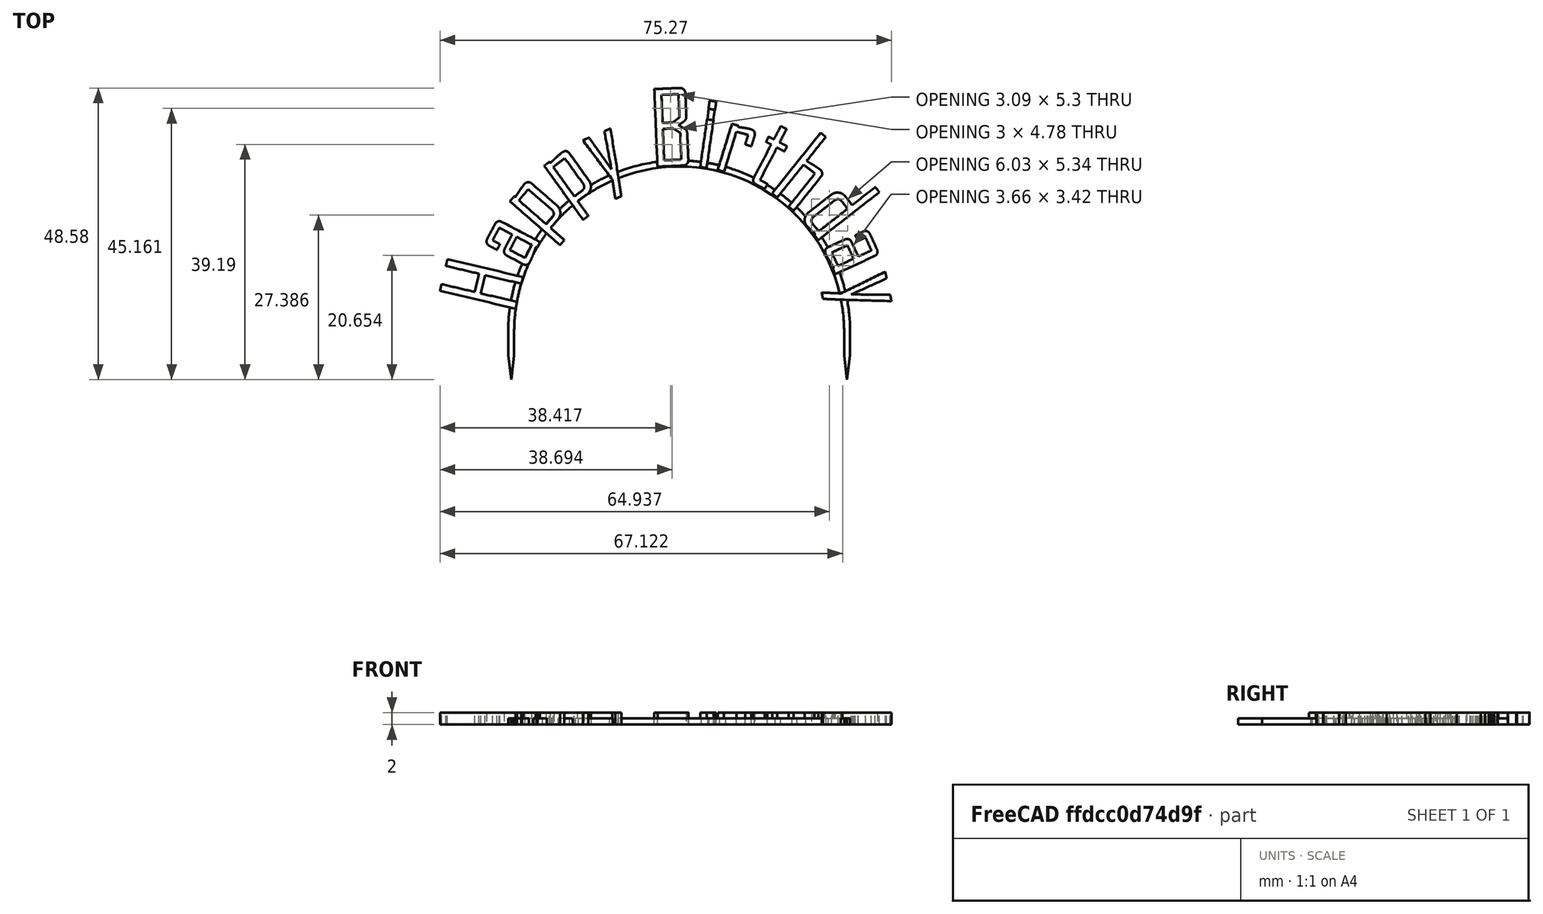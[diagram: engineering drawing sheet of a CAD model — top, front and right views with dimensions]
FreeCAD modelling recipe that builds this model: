
FCSTD DOCUMENT  (FreeCAD 0.20R29177 (Git))
Label: cake-topper-birthday
License: All rights reserved
LicenseURL: http://en.wikipedia.org/wiki/All_rights_reserved
objects: Part::Feature×21, Sketcher::SketchObject×4, PartDesign::Pad×4, App::TextDocument×1, Spreadsheet::Sheet×1, PartDesign::Plane×1, App::Part×1, PartDesign::Body×1, Mesh::Feature×1
note: 35 computed .brp shape members not serialized (recipe doc carries the construction recipe); baked Part::Feature solids carry a one-line shape summary decoded from their .brp

FEATURE [App::TextDocument] Text_document  label="Text document"
FEATURE [Spreadsheet::Sheet] Spreadsheet
  cells = A1=Text height; B1=text_h; C1(dim_text_h)==2mm; A2=Text offset x; B2=text_x; C2(dim_text_x)==-105mm; A3=Text offset y; B3=text_y; C3(dim_text_y)==177.5mm; A4=Scaffold height; B4=scaffold_h; C4(dim_scaffold_h)==1mm; A5=Scaffold width; B5=scaffold_w; C5(dim_scaffold_w)==1mm; A6=Scaffold inner radius; B6=scaffold_ir; C6(dim_scaffold_ir)==27.5mm; A7=Scaffold outer radius; B7=scaffold_or; C7(dim_scaffold_or)==dim_scaffold_ir + dim_scaffold_w; A8=Tines length; B8=tine_l; C8(dim_tine_l)==4mm; A9=Tines shaft length; B9=tine_shaft_l; C9(dim_tine_shaft_l)==4mm
FEATURE [PartDesign::Plane] DatumPlane  label="BaseXYDatumPlane"
  Length = 89.3224
  MapMode = 5
  ResizeMode = 0
  Support = -> [XY_Plane]
  Width = 79.6313
FEATURE [Part::Feature] path29548
  shape: bbox 13.84 x 8.242 x 2e-07 mm, 0 faces, 0 solids (baked)
FEATURE [Part::Feature] path29550
  shape: bbox 9.043 x 7.493 x 2e-07 mm, 0 faces, 0 solids (baked)
FEATURE [Part::Feature] path29550001
  shape: bbox 3.661 x 3.521 x 2e-07 mm, 0 faces, 0 solids (baked)
FEATURE [Part::Feature] path29552
  shape: bbox 9.091 x 10.6 x 2e-07 mm, 0 faces, 0 solids (baked)
FEATURE [Part::Feature] path29552001
  shape: bbox 5.936 x 5.828 x 2e-07 mm, 0 faces, 0 solids (baked)
FEATURE [Part::Feature] path29554
  shape: bbox 7.84 x 11.55 x 2e-07 mm, 0 faces, 0 solids (baked)
FEATURE [Part::Feature] path29554001
  shape: bbox 5.289 x 6.361 x 2e-07 mm, 0 faces, 0 solids (baked)
FEATURE [Part::Feature] path29556
  shape: bbox 6.41 x 11.71 x 2e-07 mm, 0 faces, 0 solids (baked)
FEATURE [Part::Feature] path29558
  shape: bbox 5.691 x 13.12 x 2e-07 mm, 0 faces, 0 solids (baked)
FEATURE [Part::Feature] path29558001
  shape: bbox 3.002 x 4.785 x 2e-07 mm, 0 faces, 0 solids (baked)
FEATURE [Part::Feature] path29558002
  shape: bbox 3.09 x 5.3 x 2e-07 mm, 0 faces, 0 solids (baked)
FEATURE [Part::Feature] path29560
  shape: bbox 1.303 x 1.534 x 2e-07 mm, 0 faces, 0 solids (baked)
FEATURE [Part::Feature] path29560001
  shape: bbox 2.217 x 8.117 x 2e-07 mm, 0 faces, 0 solids (baked)
FEATURE [Part::Feature] path29562
  shape: bbox 6.325 x 8.011 x 2e-07 mm, 0 faces, 0 solids (baked)
FEATURE [Part::Feature] path29564
  shape: bbox 5.756 x 10.51 x 2e-07 mm, 0 faces, 0 solids (baked)
FEATURE [Part::Feature] path29566
  shape: bbox 8.951 x 12.99 x 2e-07 mm, 0 faces, 0 solids (baked)
FEATURE [Part::Feature] path29568
  shape: bbox 12.51 x 8.831 x 2e-07 mm, 0 faces, 0 solids (baked)
FEATURE [Part::Feature] path29568001
  shape: bbox 6.149 x 5.458 x 2e-07 mm, 0 faces, 0 solids (baked)
FEATURE [Part::Feature] path29570
  shape: bbox 8.98 x 7.308 x 2e-07 mm, 0 faces, 0 solids (baked)
FEATURE [Part::Feature] path29570001
  shape: bbox 3.657 x 3.422 x 2e-07 mm, 0 faces, 0 solids (baked)
FEATURE [Part::Feature] path29572
  shape: bbox 11.65 x 4.885 x 2e-07 mm, 0 faces, 0 solids (baked)
FEATURE [App::Part] Part
  Group = -> [path29548,path29550,path29550001,path29552,path29552001,path29554,path29554001,path29556,path29558,path29558001,path29558002,path29560,path29560001,path29562,path29564,path29566,path29568,path29568001,path29570,path29570001,path29572]
  Origin = -> Origin001
  Placement = pos=(-105,177.5,0) rot=(0,0,1;0rad)
FEATURE [Sketcher::SketchObject] Sketch001  label="ArcSketch"
  FullyConstrained = true
  MapMode = 5
  Support = -> [DatumPlane]
  expr: Constraints[15] = Spreadsheet.dim_scaffold_or
  expr: Constraints[38] = Spreadsheet.dim_tine_shaft_l
  expr: Constraints[39] = Spreadsheet.dim_tine_l
  expr: Constraints[65] = Spreadsheet.dim_scaffold_or
  expr: Constraints[6] = Spreadsheet.dim_scaffold_ir
  sketch-geometry (26):
    g0: ArcOfCircle CenterX=0 CenterY=0 CenterZ=0 NormalX=0 NormalY=0 NormalZ=1 AngleXU=0 Radius=27.5 StartAngle=0 EndAngle=3.14159
    g1: LineSegment StartX=-28.5 StartY=3.5e-15 StartZ=0 EndX=-27.5 EndY=3.4e-15 EndZ=0
    g2: LineSegment StartX=27.5 StartY=0 StartZ=0 EndX=28.5 EndY=0 EndZ=0
    g3: ArcOfCircle CenterX=0 CenterY=0 CenterZ=0 NormalX=0 NormalY=0 NormalZ=1 AngleXU=0 Radius=28.5 StartAngle=1.44096 EndAngle=3.14159
    g4: ArcOfCircle CenterX=0 CenterY=0 CenterZ=0 NormalX=0 NormalY=0 NormalZ=1 AngleXU=0 Radius=28.5 StartAngle=0 EndAngle=1.40587
    g5: ArcOfCircle CenterX=0 CenterY=0 CenterZ=0 NormalX=0 NormalY=0 NormalZ=1 AngleXU=0 Radius=28.5 StartAngle=1.40587 EndAngle=1.44096
    g6: LineSegment StartX=3.69 StartY=28.2601 StartZ=0 EndX=5.12878 EndY=38.3822 EndZ=0
    g7: LineSegment StartX=4.67918 StartY=28.1133 StartZ=0 EndX=6.11883 EndY=38.2415 EndZ=0
    g8: LineSegment StartX=5.12878 StartY=38.3822 StartZ=0 EndX=6.11883 EndY=38.2415 EndZ=0
    g9: LineSegment StartX=-28.5 StartY=3.5e-15 StartZ=0 EndX=-28.5 EndY=-4 EndZ=0
    g10: LineSegment StartX=-27.5 StartY=3.4e-15 StartZ=0 EndX=-27.5 EndY=-4 EndZ=0
    g11: LineSegment StartX=-28.5 StartY=-4 StartZ=0 EndX=-28 EndY=-8 EndZ=0
    g12: LineSegment StartX=-27.5 StartY=-4 StartZ=0 EndX=-28 EndY=-8 EndZ=0
    g13: LineSegment StartX=-28.5 StartY=-4 StartZ=0 EndX=-28 EndY=-4 EndZ=0
    g14: LineSegment StartX=-28 StartY=-4 StartZ=0 EndX=-27.5 EndY=-4 EndZ=0
    g15: LineSegment StartX=-28 StartY=-4 StartZ=0 EndX=-28 EndY=-8 EndZ=0
    g16: LineSegment StartX=27.5 StartY=-4 StartZ=0 EndX=28 EndY=-4 EndZ=0
    g17: LineSegment StartX=28 StartY=-4 StartZ=0 EndX=28.5 EndY=-4 EndZ=0
    g18: LineSegment StartX=28 StartY=-4 StartZ=0 EndX=28 EndY=-8 EndZ=0
    g19: LineSegment StartX=27.5 StartY=0 StartZ=0 EndX=27.5 EndY=-4 EndZ=0
    g20: LineSegment StartX=28.5 StartY=0 StartZ=0 EndX=28.5 EndY=-4 EndZ=0
    g21: LineSegment StartX=27.5 StartY=-4 StartZ=0 EndX=28 EndY=-8 EndZ=0
    g22: LineSegment StartX=28.5 StartY=-4 StartZ=0 EndX=28 EndY=-8 EndZ=0
    g23: LineSegment StartX=3.69 StartY=28.2601 StartZ=0 EndX=0 EndY=28.2601 EndZ=0
    g24: LineSegment StartX=28.5 StartY=0 StartZ=0 EndX=28.5 EndY=28.5 EndZ=0
    g25: LineSegment StartX=28.5 StartY=28.5 StartZ=0 EndX=4.73415 EndY=28.5 EndZ=0
  constraints (71):
    c: Coincident(g0,g-1)
    c: PointOnObject(g0,g-1)
    c: PointOnObject(g0,g-1)
    c: Coincident(g4,g0)
    c: PointOnObject(g3,g-1)
    c: PointOnObject(g4,g-1)
    c: Radius(g0) = 27.5
    c: Coincident(g1,g3)
    c: Coincident(g1,g0)
    c: Coincident(g2,g0)
    c: Coincident(g2,g4)
    c: Coincident(g5,g3)
    c: Coincident(g4,g3)
    c: Coincident(g4,g5)
    c: Coincident(g4,g5)
    c: Radius(g4) = 28.5
    c: Coincident(g6,g3)
    c: Coincident(g7,g4)
    c: Coincident(g8,g6)
    c: Coincident(g8,g7)
    c: Parallel(g6,g7)
    c: Perpendicular(g8,g6)
    c: Coincident(g9,g3)
    c: Vertical(g9)
    c: Coincident(g10,g0)
    c: Vertical(g10)
    c: Coincident(g11,g9)
    c: Coincident(g12,g10)
    c: Coincident(g12,g11)
    c: Coincident(g13,g9)
    c: Horizontal(g13)
    c: Coincident(g14,g13)
    c: Coincident(g14,g10)
    c: Horizontal(g14)
    c: Coincident(g15,g13)
    c: Coincident(g15,g11)
    c: Equal(g14,g13)
    c: Vertical(g15)
    c: DistanceY(g10,g10) = 4
    c: DistanceY(g11,g10) = 4
    c: Horizontal(g16)
    c: Coincident(g17,g16)
    c: Horizontal(g17)
    c: Coincident(g18,g16)
    c: Vertical(g18)
    c: Coincident(g19,g0)
    c: Coincident(g19,g16)
    c: Vertical(g19)
    c: Coincident(g20,g4)
    c: Coincident(g20,g17)
    c: Vertical(g20)
    c: Coincident(g21,g19)
    c: Coincident(g21,g18)
    c: Coincident(g22,g20)
    c: Coincident(g22,g21)
    c: Equal(g19,g10)
    c: Equal(g18,g15)
    c: Equal(g17,g16)
    c: Distance(g8) = 1
    c: Coincident(g23,g3)
    c: PointOnObject(g23,g-2)
    c: Horizontal(g23)
    c: DistanceX(g23,g23) = 3.69
    c: Coincident(g24,g4)
    c: Vertical(g24)
    c: DistanceY(g24,g24) = 28.5
    c: Coincident(g25,g24)
    c: PointOnObject(g25,g7)
    c: Horizontal(g25)
    c: Angle(g25,g7) = 1.4296
    c: Distance(g7) = 10.23
FEATURE [Sketcher::SketchObject] Sketch  label="HappySketch"
  FullyConstrained = false
  Placement = pos=(-105,177.5,0) rot=(0,0,1;0rad)
  expr: .Placement.Base.x = Spreadsheet.dim_text_x
  expr: .Placement.Base.y = Spreadsheet.dim_text_y
  sketch-geometry (76):
    g0: BSplineCurve PolesCount=2 KnotsCount=2 Degree=1 IsPeriodic=0
    g1: BSplineCurve PolesCount=2 KnotsCount=2 Degree=1 IsPeriodic=0
    g2: BSplineCurve PolesCount=2 KnotsCount=2 Degree=1 IsPeriodic=0
    g3: BSplineCurve PolesCount=2 KnotsCount=2 Degree=1 IsPeriodic=0
    g4: BSplineCurve PolesCount=2 KnotsCount=2 Degree=1 IsPeriodic=0
    g5: BSplineCurve PolesCount=2 KnotsCount=2 Degree=1 IsPeriodic=0
    g6: BSplineCurve PolesCount=2 KnotsCount=2 Degree=1 IsPeriodic=0
    g7: BSplineCurve PolesCount=2 KnotsCount=2 Degree=1 IsPeriodic=0
    g8: BSplineCurve PolesCount=2 KnotsCount=2 Degree=1 IsPeriodic=0
    g9: BSplineCurve PolesCount=2 KnotsCount=2 Degree=1 IsPeriodic=0
    g10: BSplineCurve PolesCount=2 KnotsCount=2 Degree=1 IsPeriodic=0
    g11: BSplineCurve PolesCount=2 KnotsCount=2 Degree=1 IsPeriodic=0
    g12: BSplineCurve PolesCount=2 KnotsCount=2 Degree=1 IsPeriodic=0
    g13: BSplineCurve PolesCount=2 KnotsCount=2 Degree=1 IsPeriodic=0
    g14: BSplineCurve PolesCount=3 KnotsCount=2 Degree=2 IsPeriodic=0
    g15: BSplineCurve PolesCount=3 KnotsCount=2 Degree=2 IsPeriodic=0
    g16: BSplineCurve PolesCount=3 KnotsCount=2 Degree=2 IsPeriodic=0
    g17: BSplineCurve PolesCount=2 KnotsCount=2 Degree=1 IsPeriodic=0
    g18: BSplineCurve PolesCount=3 KnotsCount=2 Degree=2 IsPeriodic=0
    g19: BSplineCurve PolesCount=2 KnotsCount=2 Degree=1 IsPeriodic=0
    g20: BSplineCurve PolesCount=2 KnotsCount=2 Degree=1 IsPeriodic=0
    g21: BSplineCurve PolesCount=2 KnotsCount=2 Degree=1 IsPeriodic=0
    g22: BSplineCurve PolesCount=2 KnotsCount=2 Degree=1 IsPeriodic=0
    g23: BSplineCurve PolesCount=2 KnotsCount=2 Degree=1 IsPeriodic=0
    g24: BSplineCurve PolesCount=2 KnotsCount=2 Degree=1 IsPeriodic=0
    g25: BSplineCurve PolesCount=3 KnotsCount=2 Degree=2 IsPeriodic=0
    g26: BSplineCurve PolesCount=2 KnotsCount=2 Degree=1 IsPeriodic=0
    g27: BSplineCurve PolesCount=3 KnotsCount=2 Degree=2 IsPeriodic=0
    g28: BSplineCurve PolesCount=2 KnotsCount=2 Degree=1 IsPeriodic=0
    g29: BSplineCurve PolesCount=2 KnotsCount=2 Degree=1 IsPeriodic=0
    g30: BSplineCurve PolesCount=2 KnotsCount=2 Degree=1 IsPeriodic=0
    g31: BSplineCurve PolesCount=2 KnotsCount=2 Degree=1 IsPeriodic=0
    g32: BSplineCurve PolesCount=2 KnotsCount=2 Degree=1 IsPeriodic=0
    g33: BSplineCurve PolesCount=3 KnotsCount=2 Degree=2 IsPeriodic=0
    g34: BSplineCurve PolesCount=3 KnotsCount=2 Degree=2 IsPeriodic=0
    g35: BSplineCurve PolesCount=2 KnotsCount=2 Degree=1 IsPeriodic=0
    g36: BSplineCurve PolesCount=2 KnotsCount=2 Degree=1 IsPeriodic=0
    g37: BSplineCurve PolesCount=2 KnotsCount=2 Degree=1 IsPeriodic=0
    g38: BSplineCurve PolesCount=2 KnotsCount=2 Degree=1 IsPeriodic=0
    g39: BSplineCurve PolesCount=2 KnotsCount=2 Degree=1 IsPeriodic=0
    g40: BSplineCurve PolesCount=2 KnotsCount=2 Degree=1 IsPeriodic=0
    g41: BSplineCurve PolesCount=3 KnotsCount=2 Degree=2 IsPeriodic=0
    g42: BSplineCurve PolesCount=3 KnotsCount=2 Degree=2 IsPeriodic=0
    g43: BSplineCurve PolesCount=3 KnotsCount=2 Degree=2 IsPeriodic=0
    g44: BSplineCurve PolesCount=2 KnotsCount=2 Degree=1 IsPeriodic=0
    g45: BSplineCurve PolesCount=2 KnotsCount=2 Degree=1 IsPeriodic=0
    g46: BSplineCurve PolesCount=2 KnotsCount=2 Degree=1 IsPeriodic=0
    g47: BSplineCurve PolesCount=2 KnotsCount=2 Degree=1 IsPeriodic=0
    g48: BSplineCurve PolesCount=2 KnotsCount=2 Degree=1 IsPeriodic=0
    g49: BSplineCurve PolesCount=3 KnotsCount=2 Degree=2 IsPeriodic=0
    g50: BSplineCurve PolesCount=3 KnotsCount=2 Degree=2 IsPeriodic=0
    g51: BSplineCurve PolesCount=3 KnotsCount=2 Degree=2 IsPeriodic=0
    g52: BSplineCurve PolesCount=2 KnotsCount=2 Degree=1 IsPeriodic=0
    g53: BSplineCurve PolesCount=2 KnotsCount=2 Degree=1 IsPeriodic=0
    g54: BSplineCurve PolesCount=2 KnotsCount=2 Degree=1 IsPeriodic=0
    g55: BSplineCurve PolesCount=2 KnotsCount=2 Degree=1 IsPeriodic=0
    g56: BSplineCurve PolesCount=2 KnotsCount=2 Degree=1 IsPeriodic=0
    g57: BSplineCurve PolesCount=2 KnotsCount=2 Degree=1 IsPeriodic=0
    g58: BSplineCurve PolesCount=3 KnotsCount=2 Degree=2 IsPeriodic=0
    g59: BSplineCurve PolesCount=3 KnotsCount=2 Degree=2 IsPeriodic=0
    g60: BSplineCurve PolesCount=3 KnotsCount=2 Degree=2 IsPeriodic=0
    g61: BSplineCurve PolesCount=2 KnotsCount=2 Degree=1 IsPeriodic=0
    g62: BSplineCurve PolesCount=2 KnotsCount=2 Degree=1 IsPeriodic=0
    g63: BSplineCurve PolesCount=2 KnotsCount=2 Degree=1 IsPeriodic=0
    g64: BSplineCurve PolesCount=2 KnotsCount=2 Degree=1 IsPeriodic=0
    g65: BSplineCurve PolesCount=2 KnotsCount=2 Degree=1 IsPeriodic=0
    g66: BSplineCurve PolesCount=3 KnotsCount=2 Degree=2 IsPeriodic=0
    g67: BSplineCurve PolesCount=2 KnotsCount=2 Degree=1 IsPeriodic=0
    g68: BSplineCurve PolesCount=2 KnotsCount=2 Degree=1 IsPeriodic=0
    g69: BSplineCurve PolesCount=2 KnotsCount=2 Degree=1 IsPeriodic=0
    g70: BSplineCurve PolesCount=2 KnotsCount=2 Degree=1 IsPeriodic=0
    g71: BSplineCurve PolesCount=2 KnotsCount=2 Degree=1 IsPeriodic=0
    g72: BSplineCurve PolesCount=2 KnotsCount=2 Degree=1 IsPeriodic=0
    g73: BSplineCurve PolesCount=2 KnotsCount=2 Degree=1 IsPeriodic=0
    g74: BSplineCurve PolesCount=2 KnotsCount=2 Degree=1 IsPeriodic=0
    g75: BSplineCurve PolesCount=2 KnotsCount=2 Degree=1 IsPeriodic=0
  constraints (76):
    c: Coincident(g0,g1)
    c: Coincident(g1,g2)
    c: Coincident(g2,g3)
    c: Coincident(g3,g4)
    c: Coincident(g4,g5)
    c: Coincident(g5,g6)
    c: Coincident(g6,g7)
    c: Coincident(g7,g8)
    c: Coincident(g8,g9)
    c: Coincident(g9,g10)
    c: Coincident(g10,g11)
    c: Coincident(g11,g0)
    c: Coincident(g12,g13)
    c: Coincident(g13,g14)
    c: Coincident(g14,g15)
    c: Coincident(g15,g16)
    c: Coincident(g16,g17)
    c: Coincident(g17,g18)
    c: Coincident(g18,g19)
    c: Coincident(g19,g20)
    c: Coincident(g20,g21)
    c: Coincident(g21,g22)
    c: Coincident(g22,g23)
    c: Coincident(g23,g24)
    c: Coincident(g24,g25)
    c: Coincident(g25,g26)
    c: Coincident(g26,g27)
    c: Coincident(g27,g28)
    c: Coincident(g28,g12)
    c: Coincident(g29,g30)
    c: Coincident(g30,g31)
    c: Coincident(g31,g32)
    c: Coincident(g32,g29)
    c: Coincident(g33,g34)
    c: Coincident(g34,g35)
    c: Coincident(g35,g36)
    c: Coincident(g36,g37)
    c: Coincident(g37,g38)
    c: Coincident(g38,g39)
    c: Coincident(g39,g40)
    c: Coincident(g40,g41)
    c: Coincident(g41,g42)
    c: Coincident(g42,g43)
    c: Coincident(g43,g44)
    c: Coincident(g44,g33)
    c: Coincident(g45,g46)
    c: Coincident(g46,g47)
    c: Coincident(g47,g48)
    c: Coincident(g48,g49)
    c: Coincident(g49,g45)
    c: Coincident(g50,g51)
    c: Coincident(g51,g52)
    c: Coincident(g52,g53)
    c: Coincident(g53,g54)
    c: Coincident(g54,g55)
    c: Coincident(g55,g56)
    c: Coincident(g56,g57)
    c: Coincident(g57,g58)
    c: Coincident(g58,g59)
    c: Coincident(g59,g60)
    c: Coincident(g60,g61)
    c: Coincident(g61,g50)
    c: Coincident(g62,g63)
    c: Coincident(g63,g64)
    c: Coincident(g64,g65)
    c: Coincident(g65,g66)
    c: Coincident(g66,g62)
    c: Coincident(g67,g68)
    c: Coincident(g68,g69)
    c: Coincident(g69,g70)
    c: Coincident(g70,g71)
    c: Coincident(g71,g72)
    c: Coincident(g72,g73)
    c: Coincident(g73,g74)
    c: Coincident(g74,g75)
    c: Coincident(g75,g67)
FEATURE [PartDesign::Pad] Pad  label="ArcPad"
  Direction = (0,0,1)
  Length = 1
  Length2 = 10
  Profile = -> Sketch001
  ReferenceAxis = -> Sketch001 [N_Axis]
  Type = 0
  expr: Length = Spreadsheet.dim_scaffold_h
FEATURE [PartDesign::Pad] Pad001  label="HappyPad"
  BaseFeature = -> Pad
  Direction = (0,0,1)
  Length = 2
  Length2 = 10
  Profile = -> Sketch
  ReferenceAxis = -> Sketch [N_Axis]
  Type = 0
  expr: Length = Spreadsheet.dim_text_h
FEATURE [Sketcher::SketchObject] Sketch002  label="BirthdaySketch"
  FullyConstrained = false
  Placement = pos=(-105,177.5,0) rot=(0,0,1;0rad)
  expr: .Placement.Base.x = Spreadsheet.dim_text_x
  expr: .Placement.Base.y = Spreadsheet.dim_text_y
  sketch-geometry (114):
    g0: BSplineCurve PolesCount=3 KnotsCount=2 Degree=2 IsPeriodic=0
    g1: BSplineCurve PolesCount=3 KnotsCount=2 Degree=2 IsPeriodic=0
    g2: BSplineCurve PolesCount=2 KnotsCount=2 Degree=1 IsPeriodic=0
    g3: BSplineCurve PolesCount=2 KnotsCount=2 Degree=1 IsPeriodic=0
    g4: BSplineCurve PolesCount=2 KnotsCount=2 Degree=1 IsPeriodic=0
    g5: BSplineCurve PolesCount=3 KnotsCount=2 Degree=2 IsPeriodic=0
    g6: BSplineCurve PolesCount=3 KnotsCount=2 Degree=2 IsPeriodic=0
    g7: BSplineCurve PolesCount=2 KnotsCount=2 Degree=1 IsPeriodic=0
    g8: BSplineCurve PolesCount=3 KnotsCount=2 Degree=2 IsPeriodic=0
    g9: BSplineCurve PolesCount=3 KnotsCount=2 Degree=2 IsPeriodic=0
    g10: BSplineCurve PolesCount=2 KnotsCount=2 Degree=1 IsPeriodic=0
    g11: BSplineCurve PolesCount=3 KnotsCount=2 Degree=2 IsPeriodic=0
    g12: BSplineCurve PolesCount=2 KnotsCount=2 Degree=1 IsPeriodic=0
    g13: BSplineCurve PolesCount=2 KnotsCount=2 Degree=1 IsPeriodic=0
    g14: BSplineCurve PolesCount=2 KnotsCount=2 Degree=1 IsPeriodic=0
    g15: BSplineCurve PolesCount=2 KnotsCount=2 Degree=1 IsPeriodic=0
    g16: BSplineCurve PolesCount=2 KnotsCount=2 Degree=1 IsPeriodic=0
    g17: BSplineCurve PolesCount=2 KnotsCount=2 Degree=1 IsPeriodic=0
    g18: BSplineCurve PolesCount=2 KnotsCount=2 Degree=1 IsPeriodic=0
    g19: BSplineCurve PolesCount=2 KnotsCount=2 Degree=1 IsPeriodic=0
    g20: BSplineCurve PolesCount=2 KnotsCount=2 Degree=1 IsPeriodic=0
    g21: BSplineCurve PolesCount=2 KnotsCount=2 Degree=1 IsPeriodic=0
    g22: BSplineCurve PolesCount=2 KnotsCount=2 Degree=1 IsPeriodic=0
    g23: BSplineCurve PolesCount=2 KnotsCount=2 Degree=1 IsPeriodic=0
    g24: BSplineCurve PolesCount=2 KnotsCount=2 Degree=1 IsPeriodic=0
    g25: BSplineCurve PolesCount=2 KnotsCount=2 Degree=1 IsPeriodic=0
    g26: BSplineCurve PolesCount=2 KnotsCount=2 Degree=1 IsPeriodic=0
    g27: BSplineCurve PolesCount=2 KnotsCount=2 Degree=1 IsPeriodic=0
    g28: BSplineCurve PolesCount=2 KnotsCount=2 Degree=1 IsPeriodic=0
    g29: BSplineCurve PolesCount=2 KnotsCount=2 Degree=1 IsPeriodic=0
    g30: BSplineCurve PolesCount=2 KnotsCount=2 Degree=1 IsPeriodic=0
    g31: BSplineCurve PolesCount=3 KnotsCount=2 Degree=2 IsPeriodic=0
    g32: BSplineCurve PolesCount=3 KnotsCount=2 Degree=2 IsPeriodic=0
    g33: BSplineCurve PolesCount=3 KnotsCount=2 Degree=2 IsPeriodic=0
    g34: BSplineCurve PolesCount=2 KnotsCount=2 Degree=1 IsPeriodic=0
    g35: BSplineCurve PolesCount=2 KnotsCount=2 Degree=1 IsPeriodic=0
    g36: BSplineCurve PolesCount=2 KnotsCount=2 Degree=1 IsPeriodic=0
    g37: BSplineCurve PolesCount=2 KnotsCount=2 Degree=1 IsPeriodic=0
    g38: BSplineCurve PolesCount=2 KnotsCount=2 Degree=1 IsPeriodic=0
    g39: BSplineCurve PolesCount=2 KnotsCount=2 Degree=1 IsPeriodic=0
    g40: BSplineCurve PolesCount=3 KnotsCount=2 Degree=2 IsPeriodic=0
    g41: BSplineCurve PolesCount=2 KnotsCount=2 Degree=1 IsPeriodic=0
    g42: BSplineCurve PolesCount=2 KnotsCount=2 Degree=1 IsPeriodic=0
    g43: BSplineCurve PolesCount=2 KnotsCount=2 Degree=1 IsPeriodic=0
    g44: BSplineCurve PolesCount=2 KnotsCount=2 Degree=1 IsPeriodic=0
    g45: BSplineCurve PolesCount=2 KnotsCount=2 Degree=1 IsPeriodic=0
    g46: BSplineCurve PolesCount=2 KnotsCount=2 Degree=1 IsPeriodic=0
    g47: BSplineCurve PolesCount=2 KnotsCount=2 Degree=1 IsPeriodic=0
    g48: BSplineCurve PolesCount=2 KnotsCount=2 Degree=1 IsPeriodic=0
    g49: BSplineCurve PolesCount=2 KnotsCount=2 Degree=1 IsPeriodic=0
    g50: BSplineCurve PolesCount=2 KnotsCount=2 Degree=1 IsPeriodic=0
    g51: BSplineCurve PolesCount=2 KnotsCount=2 Degree=1 IsPeriodic=0
    g52: BSplineCurve PolesCount=2 KnotsCount=2 Degree=1 IsPeriodic=0
    g53: BSplineCurve PolesCount=2 KnotsCount=2 Degree=1 IsPeriodic=0
    g54: BSplineCurve PolesCount=2 KnotsCount=2 Degree=1 IsPeriodic=0
    g55: BSplineCurve PolesCount=2 KnotsCount=2 Degree=1 IsPeriodic=0
    g56: BSplineCurve PolesCount=2 KnotsCount=2 Degree=1 IsPeriodic=0
    g57: BSplineCurve PolesCount=2 KnotsCount=2 Degree=1 IsPeriodic=0
    g58: BSplineCurve PolesCount=2 KnotsCount=2 Degree=1 IsPeriodic=0
    g59: BSplineCurve PolesCount=2 KnotsCount=2 Degree=1 IsPeriodic=0
    g60: BSplineCurve PolesCount=2 KnotsCount=2 Degree=1 IsPeriodic=0
    g61: BSplineCurve PolesCount=2 KnotsCount=2 Degree=1 IsPeriodic=0
    g62: BSplineCurve PolesCount=3 KnotsCount=2 Degree=2 IsPeriodic=0
    g63: BSplineCurve PolesCount=3 KnotsCount=2 Degree=2 IsPeriodic=0
    g64: BSplineCurve PolesCount=3 KnotsCount=2 Degree=2 IsPeriodic=0
    g65: BSplineCurve PolesCount=2 KnotsCount=2 Degree=1 IsPeriodic=0
    g66: BSplineCurve PolesCount=2 KnotsCount=2 Degree=1 IsPeriodic=0
    g67: BSplineCurve PolesCount=2 KnotsCount=2 Degree=1 IsPeriodic=0
    g68: BSplineCurve PolesCount=3 KnotsCount=2 Degree=2 IsPeriodic=0
    g69: BSplineCurve PolesCount=3 KnotsCount=2 Degree=2 IsPeriodic=0
    g70: BSplineCurve PolesCount=3 KnotsCount=2 Degree=2 IsPeriodic=0
    g71: BSplineCurve PolesCount=2 KnotsCount=2 Degree=1 IsPeriodic=0
    g72: BSplineCurve PolesCount=3 KnotsCount=2 Degree=2 IsPeriodic=0
    g73: BSplineCurve PolesCount=3 KnotsCount=2 Degree=2 IsPeriodic=0
    g74: BSplineCurve PolesCount=2 KnotsCount=2 Degree=1 IsPeriodic=0
    g75: BSplineCurve PolesCount=2 KnotsCount=2 Degree=1 IsPeriodic=0
    g76: BSplineCurve PolesCount=2 KnotsCount=2 Degree=1 IsPeriodic=0
    g77: BSplineCurve PolesCount=2 KnotsCount=2 Degree=1 IsPeriodic=0
    g78: BSplineCurve PolesCount=2 KnotsCount=2 Degree=1 IsPeriodic=0
    g79: BSplineCurve PolesCount=2 KnotsCount=2 Degree=1 IsPeriodic=0
    g80: BSplineCurve PolesCount=3 KnotsCount=2 Degree=2 IsPeriodic=0
    g81: BSplineCurve PolesCount=2 KnotsCount=2 Degree=1 IsPeriodic=0
    g82: BSplineCurve PolesCount=3 KnotsCount=2 Degree=2 IsPeriodic=0
    g83: BSplineCurve PolesCount=3 KnotsCount=2 Degree=2 IsPeriodic=0
    g84: BSplineCurve PolesCount=2 KnotsCount=2 Degree=1 IsPeriodic=0
    g85: BSplineCurve PolesCount=2 KnotsCount=2 Degree=1 IsPeriodic=0
    g86: BSplineCurve PolesCount=3 KnotsCount=2 Degree=2 IsPeriodic=0
    g87: BSplineCurve PolesCount=3 KnotsCount=2 Degree=2 IsPeriodic=0
    g88: BSplineCurve PolesCount=3 KnotsCount=2 Degree=2 IsPeriodic=0
    g89: BSplineCurve PolesCount=2 KnotsCount=2 Degree=1 IsPeriodic=0
    g90: BSplineCurve PolesCount=3 KnotsCount=2 Degree=2 IsPeriodic=0
    g91: BSplineCurve PolesCount=2 KnotsCount=2 Degree=1 IsPeriodic=0
    g92: BSplineCurve PolesCount=2 KnotsCount=2 Degree=1 IsPeriodic=0
    g93: BSplineCurve PolesCount=2 KnotsCount=2 Degree=1 IsPeriodic=0
    g94: BSplineCurve PolesCount=2 KnotsCount=2 Degree=1 IsPeriodic=0
    g95: BSplineCurve PolesCount=2 KnotsCount=2 Degree=1 IsPeriodic=0
    g96: BSplineCurve PolesCount=2 KnotsCount=2 Degree=1 IsPeriodic=0
    g97: BSplineCurve PolesCount=3 KnotsCount=2 Degree=2 IsPeriodic=0
    g98: BSplineCurve PolesCount=2 KnotsCount=2 Degree=1 IsPeriodic=0
    g99: BSplineCurve PolesCount=3 KnotsCount=2 Degree=2 IsPeriodic=0
    g100: BSplineCurve PolesCount=2 KnotsCount=2 Degree=1 IsPeriodic=0
    g101: BSplineCurve PolesCount=2 KnotsCount=2 Degree=1 IsPeriodic=0
    g102: BSplineCurve PolesCount=2 KnotsCount=2 Degree=1 IsPeriodic=0
    g103: BSplineCurve PolesCount=2 KnotsCount=2 Degree=1 IsPeriodic=0
    g104: BSplineCurve PolesCount=2 KnotsCount=2 Degree=1 IsPeriodic=0
    g105: BSplineCurve PolesCount=2 KnotsCount=2 Degree=1 IsPeriodic=0
    g106: BSplineCurve PolesCount=2 KnotsCount=2 Degree=1 IsPeriodic=0
    g107: BSplineCurve PolesCount=2 KnotsCount=2 Degree=1 IsPeriodic=0
    g108: BSplineCurve PolesCount=2 KnotsCount=2 Degree=1 IsPeriodic=0
    g109: BSplineCurve PolesCount=2 KnotsCount=2 Degree=1 IsPeriodic=0
    g110: BSplineCurve PolesCount=2 KnotsCount=2 Degree=1 IsPeriodic=0
    g111: BSplineCurve PolesCount=2 KnotsCount=2 Degree=1 IsPeriodic=0
    g112: BSplineCurve PolesCount=2 KnotsCount=2 Degree=1 IsPeriodic=0
    g113: BSplineCurve PolesCount=2 KnotsCount=2 Degree=1 IsPeriodic=0
  constraints (114):
    c: Coincident(g0,g1)
    c: Coincident(g1,g2)
    c: Coincident(g2,g3)
    c: Coincident(g3,g4)
    c: Coincident(g4,g5)
    c: Coincident(g5,g6)
    c: Coincident(g6,g7)
    c: Coincident(g7,g8)
    c: Coincident(g8,g9)
    c: Coincident(g9,g10)
    c: Coincident(g10,g11)
    c: Coincident(g11,g12)
    c: Coincident(g12,g0)
    c: Coincident(g13,g14)
    c: Coincident(g14,g15)
    c: Coincident(g15,g16)
    c: Coincident(g16,g17)
    c: Coincident(g17,g13)
    c: Coincident(g18,g19)
    c: Coincident(g19,g20)
    c: Coincident(g20,g21)
    c: Coincident(g21,g22)
    c: Coincident(g22,g18)
    c: Coincident(g23,g24)
    c: Coincident(g24,g25)
    c: Coincident(g25,g26)
    c: Coincident(g26,g27)
    c: Coincident(g27,g28)
    c: Coincident(g28,g29)
    c: Coincident(g29,g30)
    c: Coincident(g30,g31)
    c: Coincident(g31,g32)
    c: Coincident(g32,g33)
    c: Coincident(g33,g34)
    c: Coincident(g34,g23)
    c: Coincident(g35,g36)
    c: Coincident(g36,g37)
    c: Coincident(g37,g38)
    c: Coincident(g38,g35)
    c: Coincident(g39,g40)
    c: Coincident(g40,g41)
    c: Coincident(g41,g42)
    c: Coincident(g42,g43)
    c: Coincident(g43,g44)
    c: Coincident(g44,g45)
    c: Coincident(g45,g46)
    c: Coincident(g46,g47)
    c: Coincident(g47,g48)
    c: Coincident(g48,g49)
    c: Coincident(g49,g50)
    c: Coincident(g50,g51)
    c: Coincident(g51,g52)
    c: Coincident(g52,g53)
    c: Coincident(g53,g39)
    c: Coincident(g54,g55)
    c: Coincident(g55,g56)
    c: Coincident(g56,g57)
    c: Coincident(g57,g58)
    c: Coincident(g58,g59)
    c: Coincident(g59,g60)
    c: Coincident(g60,g61)
    c: Coincident(g61,g62)
    c: Coincident(g62,g63)
    c: Coincident(g63,g64)
    c: Coincident(g64,g65)
    c: Coincident(g65,g54)
    c: Coincident(g66,g67)
    c: Coincident(g67,g68)
    c: Coincident(g68,g69)
    c: Coincident(g69,g70)
    c: Coincident(g70,g71)
    c: Coincident(g71,g72)
    c: Coincident(g72,g73)
    c: Coincident(g73,g74)
    c: Coincident(g74,g75)
    c: Coincident(g75,g76)
    c: Coincident(g76,g77)
    c: Coincident(g77,g66)
    c: Coincident(g78,g79)
    c: Coincident(g79,g80)
    c: Coincident(g80,g81)
    c: Coincident(g81,g82)
    c: Coincident(g82,g83)
    c: Coincident(g83,g78)
    c: Coincident(g84,g85)
    c: Coincident(g85,g86)
    c: Coincident(g86,g87)
    c: Coincident(g87,g88)
    c: Coincident(g88,g89)
    c: Coincident(g89,g90)
    c: Coincident(g90,g91)
    c: Coincident(g91,g92)
    c: Coincident(g92,g93)
    c: Coincident(g93,g94)
    c: Coincident(g94,g95)
    c: Coincident(g95,g96)
    c: Coincident(g96,g97)
    c: Coincident(g97,g98)
    c: Coincident(g98,g99)
    c: Coincident(g99,g100)
    c: Coincident(g100,g84)
    c: Coincident(g101,g102)
    c: Coincident(g102,g103)
    c: Coincident(g103,g104)
    c: Coincident(g104,g101)
    c: Coincident(g105,g106)
    c: Coincident(g106,g107)
    c: Coincident(g107,g108)
    c: Coincident(g108,g109)
    c: Coincident(g109,g110)
    c: Coincident(g110,g111)
    c: Coincident(g111,g112)
    c: Coincident(g112,g113)
    c: Coincident(g113,g105)
FEATURE [Sketcher::SketchObject] Sketch003  label="DotSketch"
  FullyConstrained = false
  Placement = pos=(-105,177.5,0) rot=(0,0,1;0rad)
  expr: .Placement.Base.x = Spreadsheet.dim_text_x
  expr: .Placement.Base.y = Spreadsheet.dim_text_y
  sketch-geometry (4):
    g0: BSplineCurve PolesCount=2 KnotsCount=2 Degree=1 IsPeriodic=0
    g1: BSplineCurve PolesCount=2 KnotsCount=2 Degree=1 IsPeriodic=0
    g2: BSplineCurve PolesCount=2 KnotsCount=2 Degree=1 IsPeriodic=0
    g3: BSplineCurve PolesCount=2 KnotsCount=2 Degree=1 IsPeriodic=0
  constraints (4):
    c: Coincident(g0,g1)
    c: Coincident(g1,g2)
    c: Coincident(g2,g3)
    c: Coincident(g3,g0)
FEATURE [PartDesign::Pad] Pad002  label="BirthdayPad"
  BaseFeature = -> Pad001
  Direction = (0,0,1)
  Length = 2
  Length2 = 10
  Profile = -> Sketch002
  ReferenceAxis = -> Sketch002 [N_Axis]
  Type = 0
  expr: Length = Spreadsheet.dim_text_h
FEATURE [PartDesign::Pad] Pad003  label="DotPad"
  BaseFeature = -> Pad002
  Direction = (0,0,1)
  Length = 2
  Length2 = 10
  Profile = -> Sketch003
  ReferenceAxis = -> Sketch003 [N_Axis]
  Type = 0
  expr: Length = Spreadsheet.dim_text_h
FEATURE [PartDesign::Body] Body
  Group = -> [DatumPlane,Sketch001,Sketch,Pad,Pad001,Sketch002,Sketch003,Pad002,Pad003]
  Origin = -> Origin
  Tip = -> Pad003
FEATURE [Mesh::Feature] Mesh  label="Body (Meshed)"
